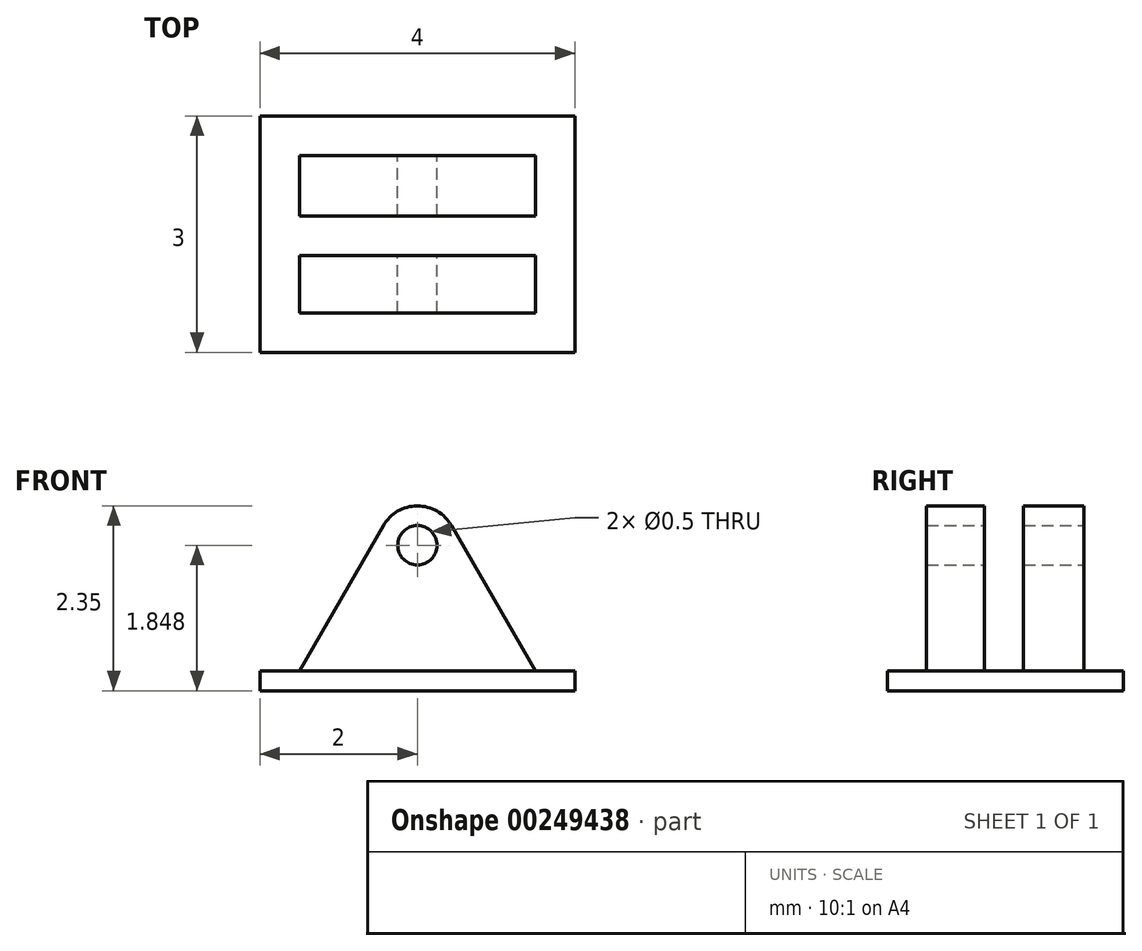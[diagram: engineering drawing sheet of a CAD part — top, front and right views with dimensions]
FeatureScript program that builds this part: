
annotation { "Feature Type Name" : "Feature", "Feature Type Description" : "" }
export const myFeature = defineFeature(function(context is Context, id is Id, definition is map)
    precondition{}
    {
        {
            var Q0;
            Q0=qCreatedBy(makeId("Top.planeOp"),FACE);
            var sketch = newSketch(context, id + "F0", { "sketchPlane" : qUnion([Q0])});
            skLineSegment(sketch, "E0.bottom", {"start": v(2, -1.5) * mm, "end": v(-2, -1.5) * mm});
            skLineSegment(sketch, "E0.top", {"start": v(2, 1.5) * mm, "end": v(-2, 1.5) * mm});
            skLineSegment(sketch, "E0.left", {"start": v(2, -1.5) * mm, "end": v(2, 1.5) * mm});
            skLineSegment(sketch, "E0.right", {"start": v(-2, -1.5) * mm, "end": v(-2, 1.5) * mm});
            skPoint(sketch, "E0.middle", {"position": v(0, 0) * mm});
            skSolve(sketch);
        }
        {
            var Q0;
            Q0=makeQuery(id+"F0.imprint","IMPRINT",FACE,{"disambiguationData":[TD([[makeQuery(id+"F0.imprint","IMPRINT",EDGE,{"derivedFrom":sQuery(id+"F0.wireOp",EDGE,"E0.bottom")}),-1.0]])]});
            extrude(context, id + "F1", {"entities" : qUnion([Q0]), "oppositeDirection" : true, "depth" : .25 * mm});
        }
        {
            var Q0;
            Q0=qCreatedBy(makeId("Front.planeOp"),FACE);
            var sketch = newSketch(context, id + "F2", { "sketchPlane" : qUnion([Q0])});
            skLineSegment(sketch, "E1", {"start": v(-1.5, 0) * mm, "end": v(1.5, 0) * mm});
            skLineSegment(sketch, "E2", {"start": v(-1.5, 0) * mm, "end": v(-0.43, 1.85) * mm});
            skLineSegment(sketch, "E3", {"start": v(0.43, 1.85) * mm, "end": v(1.5, 0) * mm});
            skArc(sketch, "E4", {"start": v(0.43, 1.85) * mm, "mid": v(0, 2.1) * mm, "end": v(-0.43, 1.85) * mm});
            skPoint(sketch, "E5.orphan", {"position": v(0, 2.6) * mm});
            skCircle(sketch, "E6", {"center": v(0, 1.6) * mm, "radius": 0.25 * mm});
            skSolve(sketch);
        }
        {
            var Q0;
            Q0=makeQuery(id+"F2.imprint","IMPRINT",FACE,{"disambiguationData":[TD([[makeQuery(id+"F2.imprint","IMPRINT",EDGE,{"derivedFrom":sQuery(id+"F2.wireOp",EDGE,"E1")}),1.0]])]});
            extrude(context, id + "F3", {"entities" : qUnion([Q0]), "operationType" : NewBodyOperationType.ADD, "endBound" : BoundingType.SYMMETRIC, "depth" : 2 * mm});
        }
        {
            var Q0;
            Q0=qCreatedBy(makeId("Right.planeOp"),FACE);
            var sketch = newSketch(context, id + "F4", { "sketchPlane" : qUnion([Q0])});
            skLineSegment(sketch, "E7.bottom", {"start": v(-0.27, 0) * mm, "end": v(0.23, 0) * mm});
            skLineSegment(sketch, "E7.top", {"start": v(-0.27, 2.12) * mm, "end": v(0.23, 2.12) * mm});
            skLineSegment(sketch, "E7.left", {"start": v(-0.27, 0) * mm, "end": v(-0.27, 2.12) * mm});
            skLineSegment(sketch, "E7.right", {"start": v(0.23, 0) * mm, "end": v(0.23, 2.12) * mm});
            skSolve(sketch);
        }
        {
            var Q0;
            Q0=makeQuery(id+"F4.imprint","IMPRINT",FACE,{"disambiguationData":[TD([[makeQuery(id+"F4.imprint","IMPRINT",EDGE,{"derivedFrom":sQuery(id+"F4.wireOp",EDGE,"E7.bottom")}),1.0]])]});
            extrude(context, id + "F5", {"entities" : qUnion([Q0]), "operationType" : NewBodyOperationType.REMOVE, "endBound" : BoundingType.SYMMETRIC, "depth" : 25 * mm});
        }
    });
